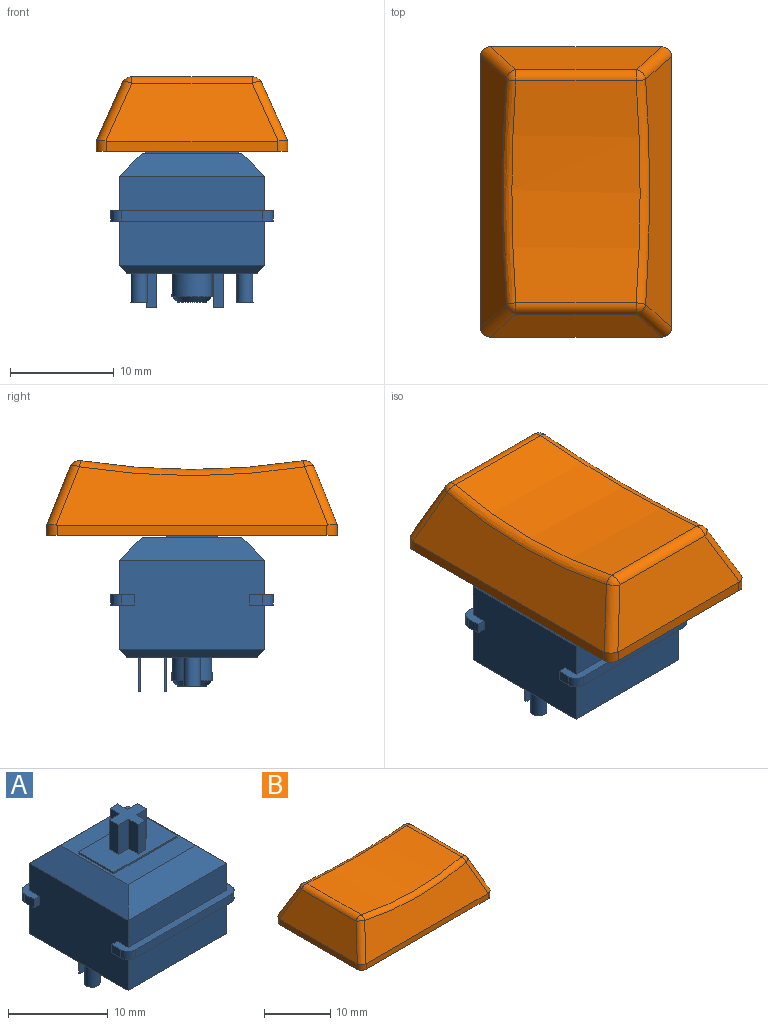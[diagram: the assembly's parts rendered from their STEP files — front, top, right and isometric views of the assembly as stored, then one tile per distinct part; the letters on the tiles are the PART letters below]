
ASSEMBLY  parts=2 mates=1
PART A: 69 faces, bbox 15.6x15.6x18.6 mm
  f0: plane 15.6x2.3mm, normal (0,0,-1), area 14.4mm2, adj f2,f3,f28,f30,f35,f60,f62,f63
  f1: plane 15.6x2.3mm, normal (0,0,-1), area 14.4mm2, adj f28,f30,f33,f34,f36,f59,f61,f64
  f2: plane 1.3x1mm, normal (1,0,0), area 1.3mm2, adj f0,f32,f62,f66
  f3: plane 1.3x1mm, normal (-1,0,0), area 1.3mm2, adj f0,f32,f63,f68
  f4: plane 15.6x2.3mm, normal (0,0,1), area 14.4mm2, adj f28,f30,f31,f33,f34,f36,f61,f64
  f5: plane 14x2.2mm, normal (-0.71,0,0.71), area 36.7mm2, adj f6,f7,f26,f30
  f6: plane 14x2.2mm, normal (0,-0.71,0.71), area 36.7mm2, adj f5,f7,f27,f31
  f7: plane 9.6x9.6mm, normal (0,0,1), area 47.2mm2, adj f5,f6,f8,f9,f10,f11,f26,f27
  f8: plane 5x0.2mm, normal (1,0,0), area 1mm2, adj f7,f9,f11,f12
  f9: plane 9x0.2mm, normal (0,1,0), area 1.8mm2, adj f7,f8,f10,f12
  f10: plane 5x0.2mm, normal (-1,0,0), area 1mm2, adj f7,f9,f11,f12
  f11: plane 9x0.2mm, normal (0,-1,0), area 1.8mm2, adj f7,f8,f10,f12
  f12: plane 9x5mm, normal (0,0,1), area 36.9mm2, adj f8,f9,f10,f11,f13,f14,f15,f16
  f13: plane 3.6x1.35mm, normal (1,0,0), area 4.9mm2, adj f12,f14,f24,f25
  f14: plane 3.6x1.08mm, normal (0,1,0), area 3.9mm2, adj f12,f13,f15,f25
  f15: plane 3.6x1.35mm, normal (-1,0,0), area 4.9mm2, adj f12,f14,f16,f25
  f16: plane 3.6x1.46mm, normal (0,1,0), area 5.3mm2, adj f12,f15,f17,f25
  f17: plane 3.6x1.3mm, normal (-1,0,0), area 4.7mm2, adj f12,f16,f18,f25
  f18: plane 3.6x1.46mm, normal (0,-1,0), area 5.3mm2, adj f12,f17,f19,f25
  f19: plane 3.6x1.35mm, normal (-1,0,0), area 4.9mm2, adj f12,f18,f20,f25
  f20: plane 3.6x1.08mm, normal (0,-1,0), area 3.9mm2, adj f12,f19,f21,f25
  f21: plane 3.6x1.35mm, normal (1,0,0), area 4.9mm2, adj f12,f20,f22,f25
  f22: plane 3.6x1.46mm, normal (0,-1,0), area 5.3mm2, adj f12,f21,f23,f25
  f23: plane 3.6x1.3mm, normal (1,0,0), area 4.7mm2, adj f12,f22,f24,f25
  f24: plane 3.6x1.46mm, normal (0,1,0), area 5.3mm2, adj f12,f13,f23,f25
  f25: plane 4x4mm, normal (0,0,1), area 8.1mm2, adj f13,f14,f15,f16,f17,f18,f19,f20
  f26: plane 14x2.2mm, normal (0,0.71,0.71), area 36.7mm2, adj f5,f7,f27,f29
  f27: plane 14x2.2mm, normal (0.71,0,0.71), area 36.7mm2, adj f6,f7,f26,f28
  f28: plane 14x8.6mm, normal (1,0,0), area 117.4mm2, adj f0,f1,f4,f27,f29,f31,f32,f55
  f29: plane 14x3.3mm, normal (0,1,0), area 46.2mm2, adj f26,f28,f30,f32
  f30: plane 14x8.6mm, normal (-1,0,0), area 117.4mm2, adj f0,f1,f4,f5,f29,f31,f32,f57
  f31: plane 14x3.3mm, normal (0,-1,0), area 46.2mm2, adj f4,f6,f28,f30
  f32: plane 15.6x2.3mm, normal (0,0,1), area 14.4mm2, adj f2,f3,f28,f29,f30,f35,f62,f63
  f33: plane 13.6x1mm, normal (0,-1,0), area 13.6mm2, adj f1,f4,f61,f64
  f34: plane 1.3x1mm, normal (1,0,0), area 1.3mm2, adj f1,f4,f61,f65
  f35: plane 13.6x1mm, normal (0,1,0), area 13.6mm2, adj f0,f32,f62,f63
  f36: plane 1.3x1mm, normal (-1,0,0), area 1.3mm2, adj f1,f4,f64,f67
  f37: plane 2.85x2.85mm, normal (0,0,-1), area 6.4mm2, adj f38
  f38: cone r=1.43mm half-angle=45deg, axis (0,0,1), area 7.4mm2, adj f37,f43
  f39: plane 1x0.2mm, normal (0,0,-1), area 0.2mm2, adj f44,f45,f46,f47
  f40: plane 1x0.2mm, normal (0,0,-1), area 0.2mm2, adj f48,f49,f50,f51
  f41: plane 1.6x1.6mm, normal (0,0,-1), area 2mm2, adj f52
  f42: plane 1.6x1.6mm, normal (0,0,-1), area 2mm2, adj f53
  f43: cylinder r=1.93mm len=3.85mm, axis (0,0,1), area 27.8mm2, adj f38,f54
  f44: plane 3.3x0.2mm, normal (-1,0,0), area 0.7mm2, adj f39,f45,f47,f54
  f45: plane 3.3x1mm, normal (0,1,0), area 3.3mm2, adj f39,f44,f46,f54
  f46: plane 3.3x0.2mm, normal (1,0,0), area 0.7mm2, adj f39,f45,f47,f54
  f47: plane 3.3x1mm, normal (0,-1,0), area 3.3mm2, adj f39,f44,f46,f54
  f48: plane 3.3x0.2mm, normal (-1,0,0), area 0.7mm2, adj f40,f49,f51,f54
  f49: plane 3.3x1mm, normal (0,1,0), area 3.3mm2, adj f40,f48,f50,f54
  f50: plane 3.3x0.2mm, normal (1,0,0), area 0.7mm2, adj f40,f49,f51,f54
  f51: plane 3.3x1mm, normal (0,-1,0), area 3.3mm2, adj f40,f48,f50,f54
  f52: cylinder r=0.8mm len=2.8mm, axis (0,0,1), area 14.1mm2, adj f41,f54
  f53: cylinder r=0.8mm len=2.8mm, axis (0,0,1), area 14.1mm2, adj f42,f54
  f54: plane 12.6x12.6mm, normal (0,0,-1), area 142.7mm2, adj f43,f44,f45,f46,f47,f48,f49,f50
  f55: plane 14x0.7mm, normal (0.71,0,-0.71), area 13.2mm2, adj f28,f54,f56,f58
  f56: plane 14x0.7mm, normal (0,0.71,-0.71), area 13.2mm2, adj f54,f55,f57,f60
  f57: plane 14x0.7mm, normal (-0.71,0,-0.71), area 13.2mm2, adj f30,f54,f56,f58
  f58: plane 14x0.7mm, normal (0,-0.71,-0.71), area 13.2mm2, adj f54,f55,f57,f59
  f59: plane 14x4.3mm, normal (0,-1,0), area 60.2mm2, adj f1,f28,f30,f58
  f60: plane 14x4.3mm, normal (0,1,0), area 60.2mm2, adj f0,f28,f30,f56
  f61: cylinder r=1mm len=1mm, axis (0,0,-1), area 1.6mm2, adj f1,f4,f33,f34
  f62: cylinder r=1mm len=1mm, axis (0,0,1), area 1.6mm2, adj f0,f2,f32,f35
  f63: cylinder r=1mm len=1mm, axis (0,0,-1), area 1.6mm2, adj f0,f3,f32,f35
  f64: cylinder r=1mm len=1mm, axis (0,0,1), area 1.6mm2, adj f1,f4,f33,f36
  f65: plane 1x0.8mm, normal (0,1,0), area 0.8mm2, adj f1,f4,f28,f34
  f66: plane 1x0.8mm, normal (0,-1,0), area 0.8mm2, adj f0,f2,f28,f32
  f67: plane 1x0.8mm, normal (0,1,0), area 0.8mm2, adj f1,f4,f30,f36
  f68: plane 1x0.8mm, normal (0,-1,0), area 0.8mm2, adj f0,f3,f30,f32
PART B: 50 faces, bbox 28x18.4x7.2 mm
  f0: plane 26.11x5.61mm, normal (0,0.91,0.41), area 133.2mm2, adj f7,f15,f18,f19,f22,f25
  f1: plane 16.55x5.57mm, normal (-0.93,0,0.37), area 84.2mm2, adj f8,f11,f14,f18,f21,f22
  f2: plane 26.11x5.61mm, normal (0,-0.91,0.41), area 133.2mm2, adj f5,f10,f11,f12,f13,f14
  f3: plane 16.55x5.57mm, normal (0.93,0,0.37), area 84.2mm2, adj f6,f10,f12,f15,f19,f20
  f4: plane 27.94x18.42mm, normal (0,0,-1), area 87.9mm2, adj f5,f6,f7,f8,f10,f11,f15,f18
  f5: plane 25.94x1mm, normal (0,-1,0), area 25.9mm2, adj f2,f4,f10,f11
  f6: plane 16.42x1mm, normal (1,0,0), area 16.4mm2, adj f3,f4,f10,f15
  f7: plane 25.94x1mm, normal (0,1,0), area 25.9mm2, adj f0,f4,f15,f18
  f8: plane 16.42x1mm, normal (-1,0,0), area 16.4mm2, adj f1,f4,f11,f18
  f9: cylinder r=68.65mm len=21.35mm, axis (0,-1,0), area 259mm2, adj f13,f20,f21,f25
  f10: cylinder r=1mm len=1.07mm, axis (0,0,1), area 1.6mm2, adj f2,f3,f4,f5,f6,f12
  f11: cylinder r=1mm len=1.07mm, axis (0,0,-1), area 1.6mm2, adj f1,f2,f4,f5,f8,f14
  f12: cylinder r=1mm len=5.78mm, axis (-0.34,0.38,0.86), area 9.3mm2, adj f2,f3,f10,f16
  f13: bspline ~21.66x1.43mm, area 24.9mm2, adj f2,f9,f16,f17
  f14: cylinder r=1mm len=5.78mm, axis (-0.34,-0.38,-0.86), area 9.3mm2, adj f1,f2,f11,f17
  f15: cylinder r=1mm len=1.07mm, axis (0,0,-1), area 1.6mm2, adj f0,f3,f4,f6,f7,f19
  f16: sphere r=1mm, area 0.9mm2, adj f12,f13,f20
  f17: sphere r=1mm, area 0.9mm2, adj f13,f14,f21
  f18: cylinder r=1mm len=1.07mm, axis (0,0,1), area 1.6mm2, adj f0,f1,f4,f7,f8,f22
  f19: cylinder r=1mm len=5.78mm, axis (0.34,0.38,-0.86), area 9.3mm2, adj f0,f3,f15,f23
  f20: cylinder r=1mm len=11.58mm, axis (0,-1,0), area 15.6mm2, adj f3,f9,f16,f23
  f21: cylinder r=1mm len=11.58mm, axis (0,-1,0), area 15.6mm2, adj f1,f9,f17,f24
  f22: cylinder r=1mm len=5.78mm, axis (0.34,-0.38,0.86), area 9.3mm2, adj f0,f1,f18,f24
  f23: sphere r=1mm, area 0.9mm2, adj f19,f20,f25
  f24: sphere r=1mm, area 0.9mm2, adj f21,f22,f25
  f25: bspline ~21.66x1.43mm, area 24.9mm2, adj f0,f9,f23,f24
  f26: plane 25.94x5.41mm, normal (0,-0.91,-0.41), area 127.6mm2, adj f27,f29,f31,f32,f33,f34
  f27: plane 16.4x5.39mm, normal (0.93,0,-0.37), area 81.1mm2, adj f26,f28,f33,f34
  f28: plane 25.94x5.41mm, normal (0,0.91,-0.41), area 127.6mm2, adj f27,f29,f30,f31,f33,f34
  f29: plane 16.4x5.39mm, normal (-0.93,0,-0.37), area 81.1mm2, adj f26,f28,f31,f34
  f30: plane 25.94x0.79mm, normal (0,1,0), area 20.4mm2, adj f4,f28,f31,f33
  f31: plane 16.42x0.81mm, normal (-1,0,0), area 13.3mm2, adj f4,f26,f28,f29,f30,f32
  f32: plane 25.94x0.79mm, normal (0,-1,0), area 20.4mm2, adj f4,f26,f31,f33
  f33: plane 16.42x0.81mm, normal (1,0,0), area 13.3mm2, adj f4,f26,f27,f28,f30,f32
  f34: cylinder r=69.65mm len=21.66mm, axis (0,-1,0), area 222.1mm2, adj f26,f27,f28,f29,f45
  f35: plane 5.35x1.9mm, normal (1,0,0), area 10.2mm2, adj f36,f44,f47,f49
  f36: plane 5.35x0.94mm, normal (0,-1,0), area 5mm2, adj f35,f37,f44,f49
  f37: plane 5.35x1.9mm, normal (-1,0,0), area 10.2mm2, adj f36,f38,f44,f49
  f38: plane 5.4x2.14mm, normal (0,-1,0), area 11.5mm2, adj f37,f39,f44,f49
  f39: plane 5.4x0.97mm, normal (-1,0,0), area 5.2mm2, adj f38,f40,f44,f49
  f40: plane 5.4x2.14mm, normal (0,1,0), area 11.5mm2, adj f39,f41,f44,f49
  f41: plane 5.35x1.9mm, normal (-1,0,0), area 10.2mm2, adj f40,f42,f44,f49
  f42: plane 5.35x0.94mm, normal (0,1,0), area 5mm2, adj f41,f43,f44,f49
  f43: plane 5.35x1.9mm, normal (1,0,0), area 10.2mm2, adj f42,f44,f46,f49
  f44: plane 7.2x7.2mm, normal (0,0,-1), area 32.1mm2, adj f35,f36,f37,f38,f39,f40,f41,f42
  f45: cylinder r=3.6mm len=7.2mm, axis (0,0,-1), area 121.9mm2, adj f34,f44
  f46: plane 5.4x2.14mm, normal (0,1,0), area 11.5mm2, adj f43,f44,f48,f49
  f47: plane 5.4x2.14mm, normal (0,-1,0), area 11.5mm2, adj f35,f44,f48,f49
  f48: plane 5.4x0.97mm, normal (1,0,0), area 5.2mm2, adj f44,f46,f47,f49
  f49: cylinder r=69.65mm len=5.22mm, axis (0,-1,0), area 8.6mm2, adj f35,f36,f37,f38,f39,f40,f41,f42
PLACE A at identity fixed
PLACE B rot(axis=(0,0,1),90deg) t=(0,0,11.7)mm
MATE fastened A.f38 <-> B.f45  axis (0,0,1) through (0,0,11.7)mm
